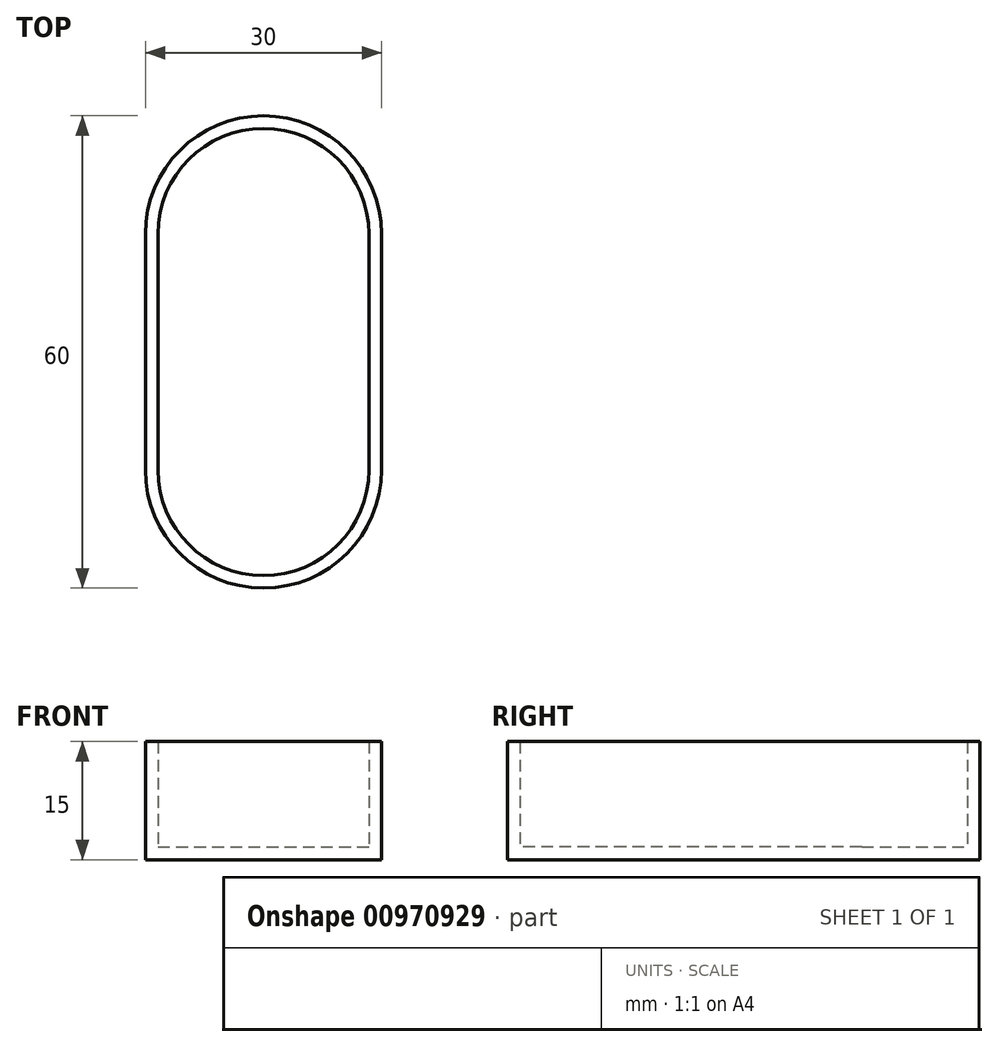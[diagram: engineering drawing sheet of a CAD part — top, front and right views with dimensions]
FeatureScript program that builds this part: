
annotation { "Feature Type Name" : "Feature", "Feature Type Description" : "" }
export const myFeature = defineFeature(function(context is Context, id is Id, definition is map)
    precondition{}
    {
        {
            var Q0;
            Q0=qCreatedBy(makeId("Top.planeOp"),FACE);
            var sketch = newSketch(context, id + "F0", { "sketchPlane" : qUnion([Q0])});
            skLineSegment(sketch, "E0.bottom", {"start": v(0, 0) * mm, "end": v(30, 0) * mm});
            skLineSegment(sketch, "E0.top", {"start": v(0, -60) * mm, "end": v(30, -60) * mm});
            skLineSegment(sketch, "E0.left", {"start": v(0, 0) * mm, "end": v(0, -15) * mm});
            skLineSegment(sketch, "E0.right", {"start": v(30, 0) * mm, "end": v(30, -15) * mm});
            skLineSegment(sketch, "E1.0", {"start": v(1.6, -15) * mm, "end": v(28.4, -15) * mm});
            skLineSegment(sketch, "E2.0", {"start": v(0, -45) * mm, "end": v(30, -45) * mm});
            skArc(sketch, "E3", {"start": v(30, -15) * mm, "mid": v(15, 0) * mm, "end": v(0, -15) * mm});
            skArc(sketch, "E4", {"start": v(0, -45) * mm, "mid": v(15, -60) * mm, "end": v(30, -45) * mm});
            skLineSegment(sketch, "E5", {"start": v(0, -15) * mm, "end": v(0, -45) * mm});
            skLineSegment(sketch, "E6", {"start": v(0, -45) * mm, "end": v(0, -60) * mm});
            skLineSegment(sketch, "E7", {"start": v(30, -15) * mm, "end": v(30, -45) * mm});
            skLineSegment(sketch, "E8", {"start": v(30, -45) * mm, "end": v(30, -60) * mm});
            skArc(sketch, "E9.0", {"start": v(28.4, -15) * mm, "mid": v(15, -1.6) * mm, "end": v(1.6, -15) * mm});
            skLineSegment(sketch, "E9.1", {"start": v(28.4, -15) * mm, "end": v(28.4, -45) * mm});
            skArc(sketch, "E9.2", {"start": v(1.6, -45) * mm, "mid": v(15, -58.4) * mm, "end": v(28.4, -45) * mm});
            skLineSegment(sketch, "E9.3", {"start": v(1.6, -15) * mm, "end": v(1.6, -45) * mm});
            skPoint(sketch, "E10.orphan", {"position": v(30, -15) * mm});
            skPoint(sketch, "E11.orphan", {"position": v(0, -15) * mm});
            skSolve(sketch);
        }
        {
            var Q0;
            {var subQ5=sQuery(id+"F0.wireOp",EDGE,"E9.0");Q0=makeQuery(id+"F0.imprint","IMPRINT",FACE,{"disambiguationData":[TD([[makeQuery(id+"F0.imprint","IMPRINT",EDGE,{"derivedFrom":subQ5}),-1.0]])]});}
            var Q1;
            {var subQ0=sQuery(id+"F0.wireOp",EDGE,"E5");Q1=makeQuery(id+"F0.imprint","IMPRINT",FACE,{"disambiguationData":[TD([[makeQuery(id+"F0.imprint","IMPRINT",EDGE,{"derivedFrom":subQ0}),1.0]])]});}
            var Q2;
            {var subQ0=sQuery(id+"F0.wireOp",EDGE,"56733db4-efbb-498f-be32-b42be4b9196b1");var subQ3=sQuery(id+"F0.wireOp",EDGE,"E9.3");var subQ5=makeQuery(id+"F0.imprint","INTERSECT",VERTEX,{"derivedFrom":[subQ0,subQ3]});Q2=makeQuery(id+"F0.imprint","IMPRINT",FACE,{"disambiguationData":[TD([[makeQuery(id+"F0.imprint","IMPRINT",EDGE,{"disambiguationData":[TD([[subQ5,1.0]])],"derivedFrom":subQ3}),-1.0]])]});}
            var Q3;
            {var subQ6=sQuery(id+"F0.wireOp",EDGE,"E9.2");Q3=makeQuery(id+"F0.imprint","IMPRINT",FACE,{"disambiguationData":[TD([[makeQuery(id+"F0.imprint","IMPRINT",EDGE,{"derivedFrom":subQ6}),-1.0]])]});}
            var Q4;
            {var subQ0=sQuery(id+"F0.wireOp",EDGE,"56733db4-efbb-498f-be32-b42be4b9196b1");var subQ3=sQuery(id+"F0.wireOp",EDGE,"E9.1");var subQ5=makeQuery(id+"F0.imprint","INTERSECT",VERTEX,{"derivedFrom":[subQ0,subQ3]});Q4=makeQuery(id+"F0.imprint","IMPRINT",FACE,{"disambiguationData":[TD([[makeQuery(id+"F0.imprint","IMPRINT",EDGE,{"disambiguationData":[TD([[subQ5,1.0]])],"derivedFrom":subQ3}),1.0]])]});}
            var Q5;
            {var subQ0=sQuery(id+"F0.wireOp",EDGE,"E7");Q5=makeQuery(id+"F0.imprint","IMPRINT",FACE,{"disambiguationData":[TD([[makeQuery(id+"F0.imprint","IMPRINT",EDGE,{"derivedFrom":subQ0}),-1.0]])]});}
            var Q6;
            {var subQ0=sQuery(id+"F0.wireOp",EDGE,"ccdc79bb-d0dc-4d7c-810d-730dc576de962");var subQ3=sQuery(id+"F0.wireOp",EDGE,"E9.1");var subQ5=makeQuery(id+"F0.imprint","INTERSECT",VERTEX,{"derivedFrom":[subQ0,subQ3]});Q6=makeQuery(id+"F0.imprint","IMPRINT",FACE,{"disambiguationData":[TD([[makeQuery(id+"F0.imprint","IMPRINT",EDGE,{"disambiguationData":[TD([[subQ5,-1.0]])],"derivedFrom":subQ3}),1.0]])]});}
            var Q7;
            {var subQ0=sQuery(id+"F0.wireOp",EDGE,"ccdc79bb-d0dc-4d7c-810d-730dc576de962");var subQ3=sQuery(id+"F0.wireOp",EDGE,"E9.3");var subQ5=makeQuery(id+"F0.imprint","INTERSECT",VERTEX,{"derivedFrom":[subQ0,subQ3]});Q7=makeQuery(id+"F0.imprint","IMPRINT",FACE,{"disambiguationData":[TD([[makeQuery(id+"F0.imprint","IMPRINT",EDGE,{"disambiguationData":[TD([[subQ5,-1.0]])],"derivedFrom":subQ3}),-1.0]])]});}
            extrude(context, id + "F1", {"entities" : qUnion([Q0, Q1, Q2, Q3, Q4, Q5, Q6, Q7]), "depth" : 15 * mm, "offsetDistance" : 25 * mm});
        }
        {
            var Q0;
            {var subQ0=sQuery(id+"F0.wireOp",EDGE,"E9.0");Q0=makeQuery(id+"F0.imprint","IMPRINT",FACE,{"disambiguationData":[TD([[makeQuery(id+"F0.imprint","IMPRINT",EDGE,{"derivedFrom":subQ0}),1.0]])]});}
            var Q1;
            {var subQ4=sQuery(id+"F0.wireOp",EDGE,"56733db4-efbb-498f-be32-b42be4b9196b1");var subQ6=sQuery(id+"F0.wireOp",EDGE,"E9.3");var subQ9=makeQuery(id+"F0.imprint","INTERSECT",VERTEX,{"derivedFrom":[subQ4,subQ6]});Q1=makeQuery(id+"F0.imprint","IMPRINT",FACE,{"disambiguationData":[TD([[makeQuery(id+"F0.imprint","IMPRINT",EDGE,{"disambiguationData":[TD([[subQ9,-1.0]])],"derivedFrom":subQ4}),1.0]])]});}
            var Q2;
            {var subQ0=sQuery(id+"F0.wireOp",EDGE,"E9.3");var subQ1=sQuery(id+"F0.wireOp",EDGE,"56733db4-efbb-498f-be32-b42be4b9196b1");var subQ2=makeQuery(id+"F0.imprint","INTERSECT",VERTEX,{"derivedFrom":[subQ1,subQ0]});Q2=makeQuery(id+"F0.imprint","IMPRINT",FACE,{"disambiguationData":[TD([[makeQuery(id+"F0.imprint","IMPRINT",EDGE,{"disambiguationData":[TD([[subQ2,-1.0]])],"derivedFrom":subQ1}),-1.0]])]});}
            var Q3;
            {var subQ0=sQuery(id+"F0.wireOp",EDGE,"ccdc79bb-d0dc-4d7c-810d-730dc576de962");var subQ1=sQuery(id+"F0.wireOp",EDGE,"56733db4-efbb-498f-be32-b42be4b9196b1");var subQ2=makeQuery(id+"F0.imprint","INTERSECT",VERTEX,{"derivedFrom":[subQ1,subQ0]});Q3=makeQuery(id+"F0.imprint","IMPRINT",FACE,{"disambiguationData":[TD([[makeQuery(id+"F0.imprint","IMPRINT",EDGE,{"disambiguationData":[TD([[subQ2,-1.0]])],"derivedFrom":subQ1}),-1.0]])]});}
            var Q4;
            {var subQ0=sQuery(id+"F0.wireOp",EDGE,"ccdc79bb-d0dc-4d7c-810d-730dc576de962");var subQ1=makeQuery(id+"F0.imprint","INTERSECT",VERTEX,{"derivedFrom":[sQuery(id+"F0.wireOp",EDGE,"56733db4-efbb-498f-be32-b42be4b9196b1"),subQ0]});Q4=makeQuery(id+"F0.imprint","IMPRINT",FACE,{"disambiguationData":[TD([[makeQuery(id+"F0.imprint","IMPRINT",EDGE,{"disambiguationData":[TD([[subQ1,1.0]])],"derivedFrom":subQ0}),1.0]])]});}
            var Q5;
            {var subQ0=sQuery(id+"F0.wireOp",EDGE,"E9.2");Q5=makeQuery(id+"F0.imprint","IMPRINT",FACE,{"disambiguationData":[TD([[makeQuery(id+"F0.imprint","IMPRINT",EDGE,{"derivedFrom":subQ0}),1.0]])]});}
            var Q6;
            Q6=makeQuery(id+"F0.imprint","IMPRINT",FACE,{"disambiguationData":[TD([[makeQuery(id+"F0.imprint","IMPRINT",EDGE,{"derivedFrom":sQuery(id+"F0.wireOp",EDGE,"E1.0")}),-1.0]])]});
            extrude(context, id + "F2", {"entities" : qUnion([Q0, Q1, Q2, Q3, Q4, Q5, Q6]), "operationType" : NewBodyOperationType.ADD, "depth" : 1.6 * mm, "offsetDistance" : 25 * mm});
        }
    });
